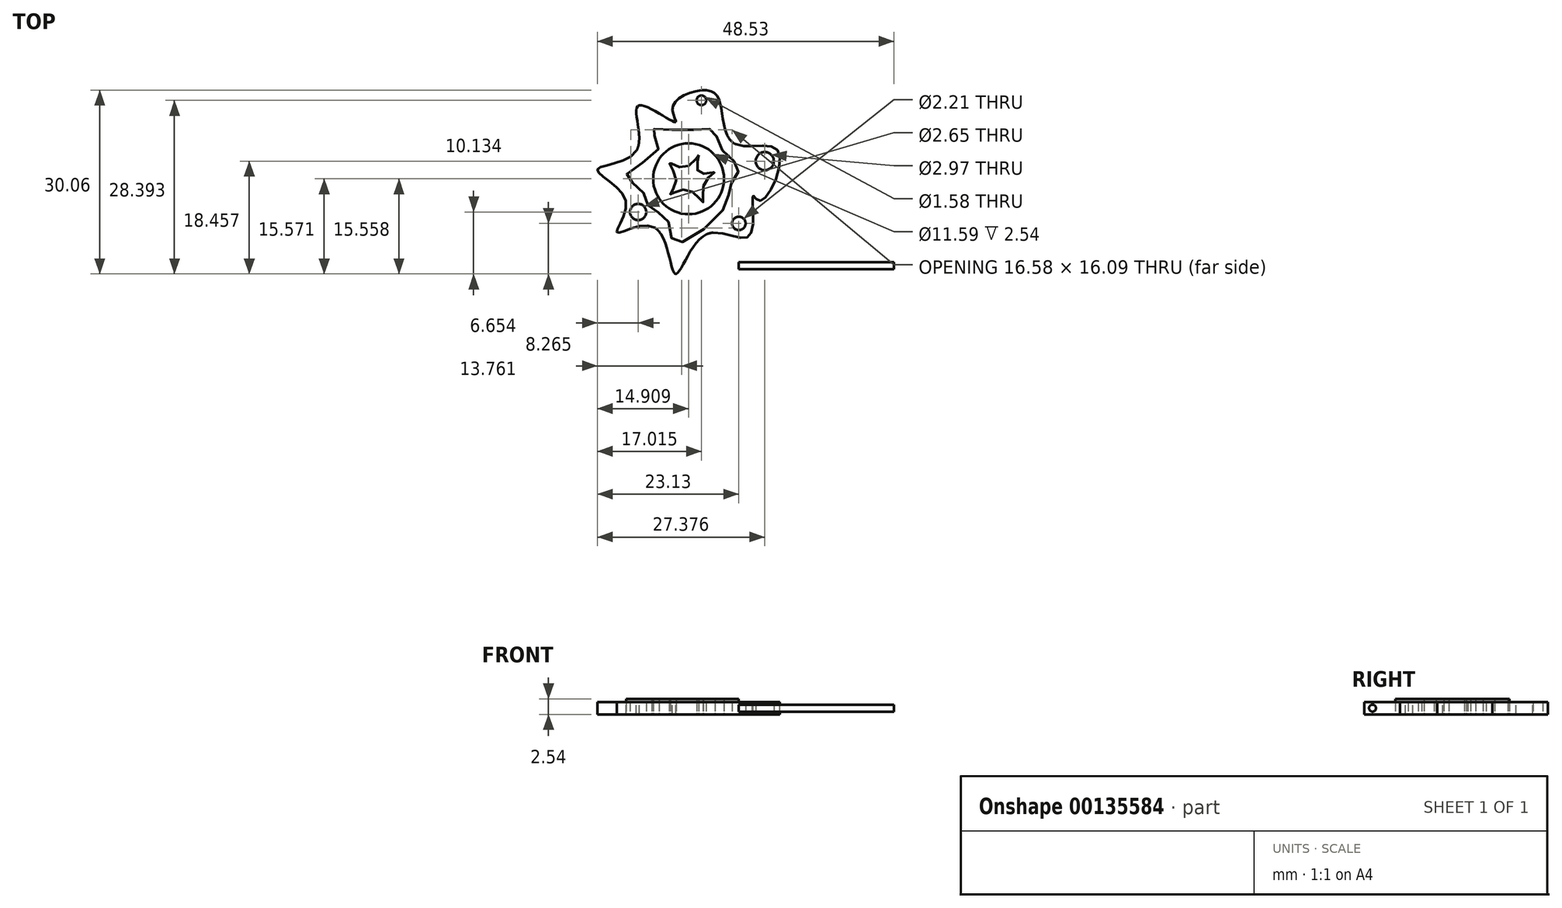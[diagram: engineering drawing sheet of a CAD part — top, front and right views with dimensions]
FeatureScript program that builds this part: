
annotation { "Feature Type Name" : "Feature", "Feature Type Description" : "" }
export const myFeature = defineFeature(function(context is Context, id is Id, definition is map)
    precondition{}
    {
        {
            var Q0;
            Q0=qCreatedBy(makeId("Top.planeOp"),FACE);
            var sketch = newSketch(context, id + "F0", { "sketchPlane" : qUnion([Q0])});
            skCircle(sketch, "E0", {"center": v(-8.22, 8.8) * mm, "radius": 5.8 * mm});
            skLineSegment(sketch, "E1.0", {"start": v(-10.36, 18.05) * mm, "end": v(-10.34, 18.05) * mm});
            skLineSegment(sketch, "E1.1", {"start": v(-1.91, 15.96) * mm, "end": v(-0.5, 14.43) * mm});
            skLineSegment(sketch, "E1.3", {"start": v(-4.18, -0.03) * mm, "end": v(-5.28, -0.28) * mm});
            skLineSegment(sketch, "E1.4", {"start": v(-12.73, -0.3) * mm, "end": v(-13.74, 0.78) * mm});
            skLineSegment(sketch, "E1.5", {"start": v(-16.76, 13.35) * mm, "end": v(-16.33, 14.77) * mm});
            skPoint(sketch, "E1.0.midPoint", {"position": v(-10.36, 18.05) * mm});
            skFitSpline(sketch, "E2", {"points": [v(-10.36, 18.05) * mm, v(-10.84, 20.54) * mm, v(-5.01, 23.23) * mm, v(-2.86, 20.27) * mm, v(-0.5, 14.43) * mm, v(6.46, 13.25) * mm, v(3.5, 5.18) * mm, v(2.3, 6.04) * mm, v(1.74, -0.53) * mm, v(-5.28, -0.28) * mm, v(-10.36, -6.77) * mm, v(-13.82, 0.83) * mm, v(-19.92, 0) * mm, v(-18.52, 5.22) * mm, v(-23.12, 10.29) * mm, v(-16.76, 13.35) * mm, v(-16.4, 20.76) * mm, v(-10.36, 18.05) * mm]});
            skPoint(sketch, "E3.orphan", {"position": v(-5.02, 19.28) * mm});
            skPoint(sketch, "E4.orphan", {"position": v(2.47, 11.26) * mm});
            skArc(sketch, "E5.trimOffspring", {"start": v(-10.34, 18.05) * mm, "mid": v(-10.35, 18.05) * mm, "end": v(-10.36, 18.05) * mm, "construction": true});
            skArc(sketch, "E6.trimOffspring", {"start": v(-0.62, 14.5) * mm, "mid": v(-1.21, 15.2) * mm, "end": v(-1.86, 15.85) * mm, "construction": true});
            skPoint(sketch, "E7.orphan", {"position": v(-18.9, 6.32) * mm});
            skPoint(sketch, "E8.orphan", {"position": v(-15.7, 16.81) * mm});
            skPoint(sketch, "E9.0.midPoint", {"position": v(-4.16, 16.69) * mm});
            skPoint(sketch, "E9.0.end.orphan", {"position": v(0.2, 15.47) * mm});
            skPoint(sketch, "E10.orphan", {"position": v(-16.26, 13.09) * mm});
            skPoint(sketch, "E9.5.end.orphan", {"position": v(-8.52, 17.9) * mm});
            skFitSpline(sketch, "E11", {"points": [v(-2.72, 13.46) * mm, v(-4.16, 16.69) * mm, v(-8.83, 16.69) * mm, v(-14.27, 16.69) * mm, v(-13.08, 13.88) * mm, v(-18.43, 9.38) * mm, v(-15.97, 7.1) * mm, v(-14.6, 4.12) * mm, v(-11.72, 2.16) * mm, v(-10.45, -1.66) * mm, v(-2.2, 4.29) * mm, v(-1.44, 7.6) * mm, v(0, 10.49) * mm, v(-2.72, 13.46) * mm]});
            skCircle(sketch, "E12", {"center": v(4.25, 11.68) * mm, "radius": 1.49 * mm});
            skCircle(sketch, "E13", {"center": v(-16.48, 3.35) * mm, "radius": 1.33 * mm});
            skCircle(sketch, "E14", {"center": v(0, 1.49) * mm, "radius": 1.1 * mm});
            skCircle(sketch, "E15", {"center": v(-6.11, 21.61) * mm, "radius": 0.79 * mm});
            skFitSpline(sketch, "E16", {"points": [v(-6.54, 12.66) * mm, v(-8.66, 10.66) * mm, v(-11.38, 11.42) * mm, v(-10.28, 8.53) * mm, v(-11.21, 6.24) * mm, v(-8.32, 7) * mm, v(-5.86, 4.97) * mm, v(-5.6, 8.2) * mm, v(-3.9, 9.9) * mm, v(-6.62, 9.9) * mm, v(-6.54, 12.66) * mm]});
            skPoint(sketch, "E17.cCircle.end.orphan", {"position": v(-3.9, 12.66) * mm});
            skLineSegment(sketch, "E18", {"start": v(-5.01, 23.23) * mm, "end": v(20.04, 23.23) * mm, "construction": true});
            skLineSegment(sketch, "E19", {"start": v(-10.36, -6.77) * mm, "end": v(22.25, -6.77) * mm, "construction": true});
            skSolve(sketch);
        }
        {
            var Q0;
            Q0=makeQuery(id+"F0.imprint","IMPRINT",FACE,{"disambiguationData":[TD([[makeQuery(id+"F0.imprint","IMPRINT",EDGE,{"derivedFrom":sQuery(id+"F0.wireOp",EDGE,"E11")}),-1.0]])]});
            var Q1;
            Q1=makeQuery(id+"F0.imprint","IMPRINT",FACE,{"disambiguationData":[TD([[makeQuery(id+"F0.imprint","IMPRINT",EDGE,{"derivedFrom":sQuery(id+"F0.wireOp",EDGE,"E0")}),1.0]])]});
            extrude(context, id + "F1", {"entities" : qUnion([Q0, Q1]), "depth" : 2 * mm});
        }
        {
            var Q0;
            Q0=makeQuery(id+"F0.imprint","IMPRINT",FACE,{"disambiguationData":[TD([[makeQuery(id+"F0.imprint","IMPRINT",EDGE,{"derivedFrom":sQuery(id+"F0.wireOp",EDGE,"E0")}),-1.0]])]});
            var Q1;
            Q1=makeQuery(id+"F0.imprint","IMPRINT",FACE,{"disambiguationData":[TD([[makeQuery(id+"F0.imprint","IMPRINT",EDGE,{"derivedFrom":sQuery(id+"F0.wireOp",EDGE,"E16")}),1.0]])]});
            extrude(context, id + "F2", {"entities" : qUnion([Q0, Q1]), "depth" : 2.54 * mm});
        }
        {
            var Q0;
            Q0=qCreatedBy(makeId("Right.planeOp"),FACE);
            var sketch = newSketch(context, id + "F3", { "sketchPlane" : qUnion([Q0])});
            skPoint(sketch, "E20.end.orphan", {"position": v(-6.72, 1.95) * mm});
            skLineSegment(sketch, "E21", {"start": v(-11.7, 0) * mm, "end": v(-11.7, 0) * mm});
            skPoint(sketch, "E22.start.orphan", {"position": v(-8.38, 1.95) * mm});
            skPoint(sketch, "E23.start.orphan", {"position": v(-6.72, 0) * mm});
            skCircle(sketch, "E24", {"center": v(-5.43, 1.03) * mm, "radius": 0.57 * mm});
            skSolve(sketch);
        }
        {
            var Q0;
            Q0 = qSketchRegion(id + "F3", true);
            extrude(context, id + "F4", {"entities" : qUnion([Q0]), "depth" : 25.4 * mm});
        }
    });
